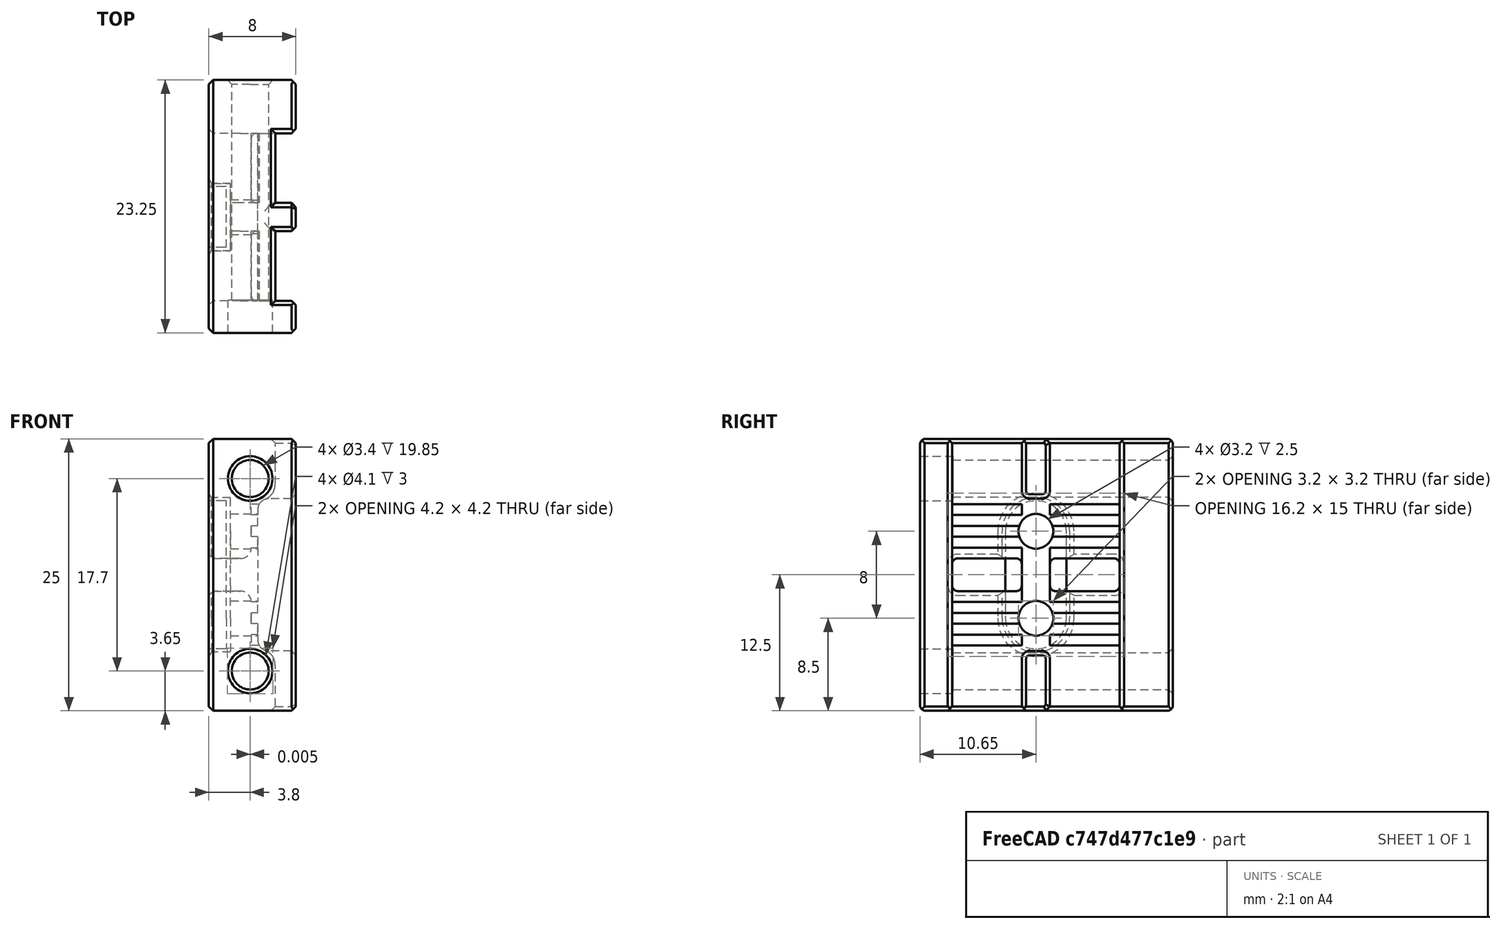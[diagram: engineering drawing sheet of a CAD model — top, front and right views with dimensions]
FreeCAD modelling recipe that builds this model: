
FCSTD DOCUMENT  (FreeCAD 0.18R16146 (Git))
Label: belt-mounter-mod
License: All rights reserved
LicenseURL: http://en.wikipedia.org/wiki/All_rights_reserved
objects: Part::Feature×6, Part::Cut×5, Part::Cylinder×4, Part::Box×3, Part::MultiFuse×3, Part::Chamfer×1
note: 22 computed .brp shape members not serialized (recipe doc carries the construction recipe); baked Part::Feature solids carry a one-line shape summary decoded from their .brp

FEATURE [Part::Feature] Part__Feature164  label="Retension_Block001"
  Placement = pos=(16.5,34,-2.8e-14) rot=(0.57735,-0.57735,0.57735;2.0944rad)
  shape: bbox 8 x 23.25 x 25 mm, 185 faces (baked)
FEATURE [Part::Feature] Part__Feature163  label="Retension_Block"
  Placement = pos=(16.5,34,-2.8e-14) rot=(0.57735,-0.57735,0.57735;2.0944rad)
  shape: bbox 1.4 x 5.6 x 13.6 mm, 6 faces (baked)
FEATURE [Part::Cylinder] Cylinder
  Angle = 360
  AttacherType = Attacher::AttachEngine3D
  Height = 2.55
  Placement = pos=(17.3,9.75,-8.85) rot=(1,0,0;4.71239rad)
  Radius = 3.6
FEATURE [Part::Cylinder] Cylinder002
  Angle = 360
  AttacherType = Attacher::AttachEngine3D
  Height = 3
  Placement = pos=(17.305,9.75,8.85) rot=(-1,0,0;1.5708rad)
  Radius = 2.05
FEATURE [Part::Cylinder] Cylinder003
  Angle = 360
  AttacherType = Attacher::AttachEngine3D
  Height = 3
  Placement = pos=(17.3,9.75,-8.85) rot=(-1,0,0;1.5708rad)
  Radius = 2.05
FEATURE [Part::Cylinder] Cylinder001
  Angle = 360
  AttacherType = Attacher::AttachEngine3D
  Height = 2.55
  Placement = pos=(17.305,9.75,8.85) rot=(-1,0,0;1.5708rad)
  Radius = 3.6
FEATURE [Part::Box] Box  label="Cube"
  AttacherType = Attacher::AttachEngine3D
  Height = 10
  Length = 10
  Placement = pos=(12,4,-21.9) rot=(0,0,1;0rad)
  Width = 10
FEATURE [Part::Box] Box001  label="Cube001"
  AttacherType = Attacher::AttachEngine3D
  Height = 10
  Length = 10
  Placement = pos=(12,4,11.9) rot=(0,0,1;0rad)
  Width = 10
FEATURE [Part::Cut] Cut
  Base = -> Cylinder001
  Tool = -> Box001
FEATURE [Part::Cut] Cut001
  Base = -> Cylinder
  Tool = -> Box
FEATURE [Part::Box] Box002  label="Cube002"
  AttacherType = Attacher::AttachEngine3D
  Height = 29
  Length = 10
  Placement = pos=(3.9,0.15,-14) rot=(0,0,1;0rad)
  Width = 10
FEATURE [Part::Chamfer] Chamfer
  Base = -> Box002
  Edges = 1 edges r=0.4: [Edge7]
FEATURE [Part::Feature] Chamfer001
  shape: bbox 10 x 10 x 29 mm, 7 faces (baked)
FEATURE [Part::Cut] Cut002
  Base = -> Cut
  Tool = -> Chamfer
FEATURE [Part::Cut] Cut003
  Base = -> Cut001
  Tool = -> Chamfer001
FEATURE [Part::MultiFuse] Fusion
  Shapes = -> [Cylinder002,Cylinder003]
FEATURE [Part::MultiFuse] Fusion001
  Shapes = -> [Cut003,Cut002,Part__Feature164]
FEATURE [Part::Cut] Cut004
  Base = -> Fusion001
  Tool = -> Fusion
FEATURE [Part::Feature] Part__Feature165  label="Retension_Block002"
  Placement = pos=(16.7,34,-2.8e-14) rot=(0.57735,-0.57735,0.57735;2.0944rad)
  shape: bbox 1.4 x 5.6 x 13.6 mm, 6 faces (baked)
FEATURE [Part::MultiFuse] Fusion002  label="custom-support"
  Shapes = -> [Part__Feature165,Part__Feature163]
FEATURE [Part::Feature] Cut004001  label="Cut005"
  shape: bbox 8 x 23.25 x 25 mm, 175 faces (baked)
FEATURE [Part::Feature] Fusion002001  label="custom-support001"
  shape: bbox 1.6 x 5.6 x 13.6 mm, 6 faces (baked)
